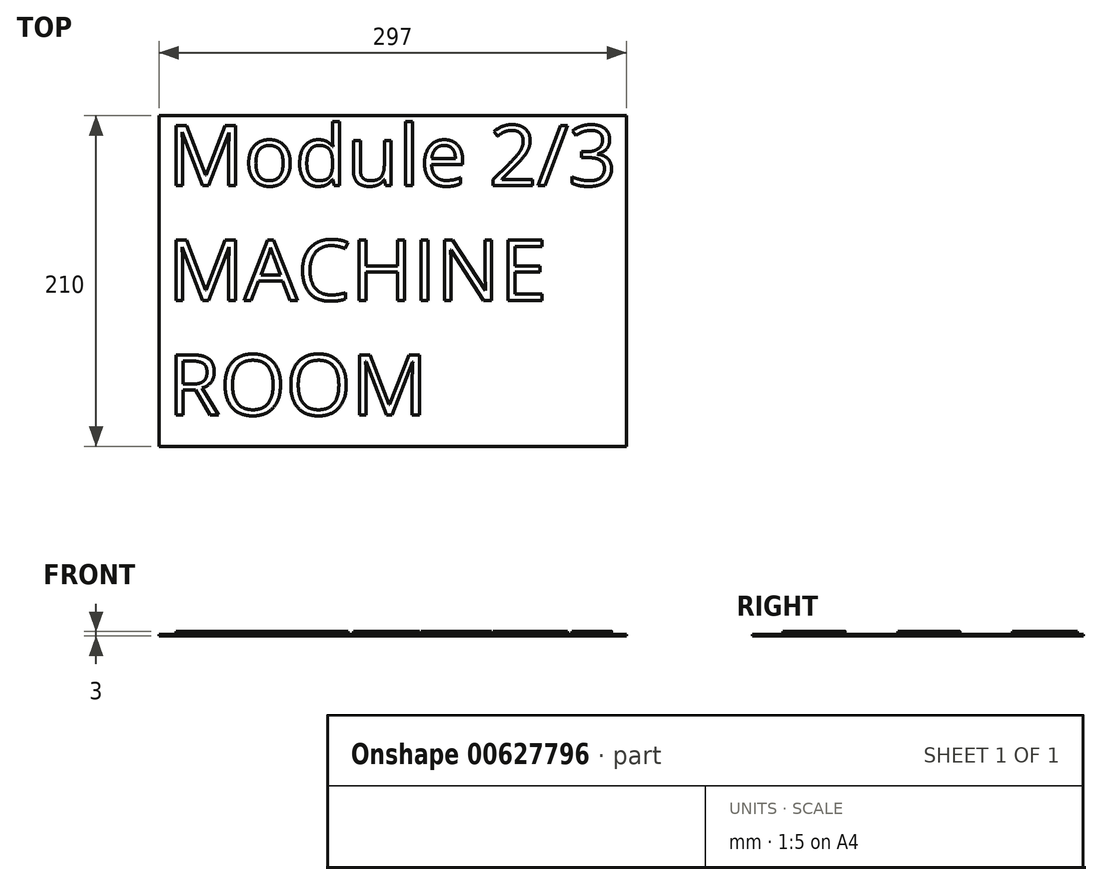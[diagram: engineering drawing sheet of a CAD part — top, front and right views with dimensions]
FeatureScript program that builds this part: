
annotation { "Feature Type Name" : "Feature", "Feature Type Description" : "" }
export const myFeature = defineFeature(function(context is Context, id is Id, definition is map)
    precondition{}
    {
        {
            var Q0;
            Q0=qCreatedBy(makeId("Top.planeOp"),FACE);
            var sketch = newSketch(context, id + "F0", { "sketchPlane" : qUnion([Q0])});
            skLineSegment(sketch, "E0.bottom", {"start": v(-195.9, 139.38) * mm, "end": v(101.1, 139.38) * mm});
            skLineSegment(sketch, "E0.top", {"start": v(-195.9, -70.62) * mm, "end": v(101.1, -70.62) * mm});
            skLineSegment(sketch, "E0.left", {"start": v(-195.9, 139.38) * mm, "end": v(-195.9, -70.62) * mm});
            skLineSegment(sketch, "E0.right", {"start": v(101.1, 139.38) * mm, "end": v(101.1, -70.62) * mm});
            skSolve(sketch);
        }
        {
            var Q0;
            Q0=qSketchRegion(id+"F0",true);
            extrude(context, id + "F1", {"entities" : qUnion([Q0]), "depth" : 1 * mm, "offsetDistance" : 25 * mm});
        }
        {
            var Q0;
            Q0=makeQuery(id+"F1.opExtrude","CAP_FACE",FACE,{"disambiguationData":[OSD([sQuery(id+"F0.wireOp",EDGE,"E0.bottom"),sQuery(id+"F0.wireOp",EDGE,"E0.top"),sQuery(id+"F0.wireOp",EDGE,"E0.left"),sQuery(id+"F0.wireOp",EDGE,"E0.right")])],"isStart":false});
            var sketch = newSketch(context, id + "F2", { "sketchPlane" : qUnion([Q0])});
            skText(sketch, "E1", { "text": "Module 2/3\nMACHINE\nROOM", "fontName": "OpenSans-Regular.ttf"});
            const initialGuessF2  = {"E1": [-0.19035, 0.095, 1, 0, 0.03858]};
            skSetInitialGuess(sketch, initialGuessF2);
            skSolve(sketch);
        }
        {
            var Q0;
            Q0=qSketchRegion(id+"F2",true);
            extrude(context, id + "F3", {"entities" : qUnion([Q0]), "operationType" : NewBodyOperationType.ADD, "depth" : 2 * mm, "offsetDistance" : 25 * mm});
        }
    });
